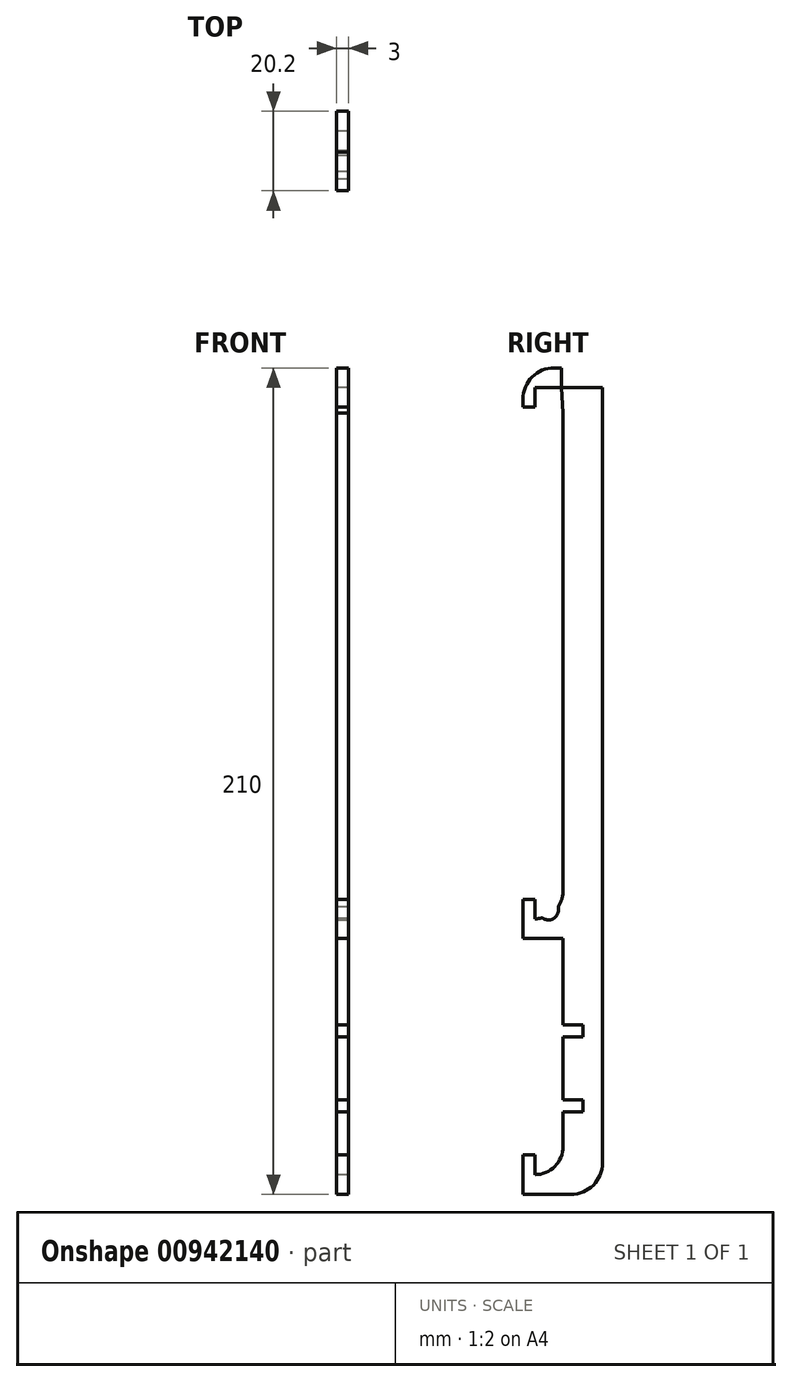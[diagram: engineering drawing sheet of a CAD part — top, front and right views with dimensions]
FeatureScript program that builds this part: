
annotation { "Feature Type Name" : "Feature", "Feature Type Description" : "" }
export const myFeature = defineFeature(function(context is Context, id is Id, definition is map)
    precondition{}
    {
        {
            var Q0;
            Q0=qCreatedBy(makeId("Right.planeOp"),FACE);
            var sketch = newSketch(context, id + "F0", { "sketchPlane" : qUnion([Q0])});
            skLineSegment(sketch, "E0.bottom", {"start": v(3, 0) * mm, "end": v(10.2, 0) * mm});
            skLineSegment(sketch, "E0.top", {"start": v(3, 100) * mm, "end": v(3, 100) * mm});
            skLineSegment(sketch, "E0.left", {"start": v(3, 0) * mm, "end": v(3, 100) * mm});
            skLineSegment(sketch, "E0.right", {"start": v(10.2, 0) * mm, "end": v(10.2, 92.8) * mm});
            skPoint(sketch, "E1.visualSharp", {"position": v(10.2, 100) * mm});
            skArc(sketch, "E1.filletArc", {"start": v(10.2, 92.8) * mm, "mid": v(8.1, 97.9) * mm, "end": v(3, 100) * mm});
            skLineSegment(sketch, "E2.bottom", {"start": v(0, 0) * mm, "end": v(20.2, 0) * mm});
            skLineSegment(sketch, "E2.top", {"start": v(0, 105) * mm, "end": v(20.2, 105) * mm});
            skLineSegment(sketch, "E2.left", {"start": v(0, 0) * mm, "end": v(0, 105) * mm});
            skLineSegment(sketch, "E2.right", {"start": v(20.2, 0) * mm, "end": v(20.2, 105) * mm});
            skLineSegment(sketch, "E3", {"start": v(0, 95) * mm, "end": v(3, 95) * mm});
            skLineSegment(sketch, "E4.bottom", {"start": v(10.2, 84) * mm, "end": v(15.2, 84) * mm});
            skLineSegment(sketch, "E4.top", {"start": v(10.2, 81) * mm, "end": v(15.2, 81) * mm});
            skLineSegment(sketch, "E4.left", {"start": v(10.2, 84) * mm, "end": v(10.2, 81) * mm});
            skLineSegment(sketch, "E4.right", {"start": v(15.2, 84) * mm, "end": v(15.2, 81) * mm});
            skLineSegment(sketch, "E5.bottom", {"start": v(10.2, 65) * mm, "end": v(15.2, 65) * mm});
            skLineSegment(sketch, "E5.top", {"start": v(10.2, 62) * mm, "end": v(15.2, 62) * mm});
            skLineSegment(sketch, "E5.left", {"start": v(10.2, 65) * mm, "end": v(10.2, 62) * mm});
            skLineSegment(sketch, "E5.right", {"start": v(15.2, 65) * mm, "end": v(15.2, 62) * mm});
            skSolve(sketch);
        }
        {
            var Q0;
            {var subQ1=sQuery(id+"F0.wireOp",EDGE,"E0.right");Q0=makeQuery(id+"F0.imprint","IMPRINT",FACE,{"disambiguationData":[TD([[makeQuery(id+"F0.imprint","IMPRINT",EDGE,{"derivedFrom":subQ1}),-1.0]])]});}
            extrude(context, id + "F1", {"entities" : qUnion([Q0]), "depth" : 3 * mm, "offsetDistance" : 25 * mm});
        }
        {
            var Q0;
            Q0=makeQuery(id+"F1.opExtrude","SWEPT_BODY",BODY,{"disambiguationData":[OSD([sQuery(id+"F0.wireOp",EDGE,"E0.left"),sQuery(id+"F0.wireOp",EDGE,"E0.right"),sQuery(id+"F0.wireOp",EDGE,"E1.filletArc"),sQuery(id+"F0.wireOp",EDGE,"E2.bottom"),sQuery(id+"F0.wireOp",EDGE,"E2.top"),sQuery(id+"F0.wireOp",EDGE,"E2.left"),sQuery(id+"F0.wireOp",EDGE,"E2.right"),sQuery(id+"F0.wireOp",EDGE,"E3")])]});
            var Q1;
            Q1=qCreatedBy(makeId("Top.planeOp"),FACE);
            mirror(context, id + "F2", {"operationType" : NewBodyOperationType.ADD, "entities" : qUnion([Q0]), "mirrorPlane" : qUnion([Q1])});
        }
        {
            var Q0;
            Q0=qCreatedBy(makeId("Right.planeOp"),FACE);
            var sketch = newSketch(context, id + "F3", { "sketchPlane" : qUnion([Q0])});
            skArc(sketch, "E6.0", {"start": v(10.2, 92.8) * mm, "mid": v(8.1, 97.9) * mm, "end": v(3, 100) * mm});
            skLineSegment(sketch, "E7.0", {"start": v(3, 0) * mm, "end": v(3, 100) * mm});
            skLineSegment(sketch, "E8.0", {"start": v(0, 95) * mm, "end": v(3, 95) * mm});
            skLineSegment(sketch, "E9.0", {"start": v(0, 0) * mm, "end": v(0, 105) * mm});
            skLineSegment(sketch, "E10.0", {"start": v(0, 105) * mm, "end": v(20.2, 105) * mm});
            skLineSegment(sketch, "E11.0", {"start": v(10.2, 0) * mm, "end": v(10.2, 92.8) * mm});
            skLineSegment(sketch, "E12.0", {"start": v(20.2, 0) * mm, "end": v(20.2, 105) * mm});
            skLineSegment(sketch, "E13.0", {"start": v(15.2, 84) * mm, "end": v(15.2, 81) * mm});
            skLineSegment(sketch, "E14", {"start": v(15.2, 84) * mm, "end": v(20.2, 84) * mm});
            skLineSegment(sketch, "E15", {"start": v(15.2, 81) * mm, "end": v(20.2, 81) * mm});
            skLineSegment(sketch, "E16", {"start": v(10.2, 32.5) * mm, "end": v(20.2, 32.5) * mm});
            skSolve(sketch);
        }
        {
            var Q0;
            {var subQ6=sQuery(id+"F3.wireOp",EDGE,"E6.0");Q0=makeQuery(id+"F3.imprint","IMPRINT",FACE,{"disambiguationData":[TD([[makeQuery(id+"F3.imprint","IMPRINT",EDGE,{"derivedFrom":subQ6}),-1.0]])]});}
            extrude(context, id + "F4", {"entities" : qUnion([Q0]), "depth" : 3 * mm, "offsetDistance" : 25 * mm});
        }
        {
            var Q0;
            Q0=makeQuery(id+"F4.opExtrude","SWEPT_BODY",BODY,{"disambiguationData":[OSD([sQuery(id+"F3.wireOp",EDGE,"E6.0"),sQuery(id+"F3.wireOp",EDGE,"E7.0"),sQuery(id+"F3.wireOp",EDGE,"E8.0"),sQuery(id+"F3.wireOp",EDGE,"E9.0"),sQuery(id+"F3.wireOp",EDGE,"E10.0"),sQuery(id+"F3.wireOp",EDGE,"E11.0"),sQuery(id+"F3.wireOp",EDGE,"E12.0"),sQuery(id+"F3.wireOp",EDGE,"E13.0"),sQuery(id+"F3.wireOp",EDGE,"E14"),sQuery(id+"F3.wireOp",EDGE,"E15"),sQuery(id+"F3.wireOp",EDGE,"E16")])]});
            var Q1;
            Q1=makeQuery(id+"F4.opExtrude","SWEPT_FACE",FACE,{"disambiguationData":[OSD([sQuery(id+"F3.wireOp",EDGE,"E16")])]});
            mirror(context, id + "F5", {"operationType" : NewBodyOperationType.ADD, "entities" : qUnion([Q0]), "mirrorPlane" : qUnion([Q1])});
        }
        {
            var Q0;
            Q0=qCreatedBy(makeId("Right.planeOp"),FACE);
            var sketch = newSketch(context, id + "F6", { "sketchPlane" : qUnion([Q0])});
            skLineSegment(sketch, "E17.0", {"start": v(0, 105) * mm, "end": v(20.2, 105) * mm});
            skCircle(sketch, "E18", {"center": v(21, 113) * mm, "radius": 2.6 * mm});
            skCircle(sketch, "E19", {"center": v(21, 113) * mm, "radius": 6.75 * mm});
            skLineSegment(sketch, "E20", {"start": v(0, 105) * mm, "end": v(16.81, 118.3) * mm});
            skLineSegment(sketch, "E21", {"start": v(20.2, 105) * mm, "end": v(24.08, 107) * mm});
            skSolve(sketch);
        }
        {
            var Q0;
            Q0=makeQuery(id+"F6.imprint","IMPRINT",FACE,{"disambiguationData":[TD([[makeQuery(id+"F6.imprint","IMPRINT",EDGE,{"derivedFrom":sQuery(id+"F6.wireOp",EDGE,"E17.0")}),1.0]])]});
            var Q1;
            Q1=makeQuery(id+"F6.imprint","IMPRINT",FACE,{"disambiguationData":[TD([[makeQuery(id+"F6.imprint","IMPRINT",EDGE,{"derivedFrom":sQuery(id+"F6.wireOp",EDGE,"E18")}),-1.0]])]});
            var Q2;
            {var subQ0=makeQuery(id+"F4.opExtrude","CAP_FACE",FACE,{"disambiguationData":[OSD([sQuery(id+"F3.wireOp",EDGE,"E6.0"),sQuery(id+"F3.wireOp",EDGE,"E7.0"),sQuery(id+"F3.wireOp",EDGE,"E8.0"),sQuery(id+"F3.wireOp",EDGE,"E9.0"),sQuery(id+"F3.wireOp",EDGE,"E10.0"),sQuery(id+"F3.wireOp",EDGE,"E11.0"),sQuery(id+"F3.wireOp",EDGE,"E12.0"),sQuery(id+"F3.wireOp",EDGE,"E13.0"),sQuery(id+"F3.wireOp",EDGE,"E14"),sQuery(id+"F3.wireOp",EDGE,"E15"),sQuery(id+"F3.wireOp",EDGE,"E16")])],"isStart":false});Q2=makeQuery(id+"F5.boolean.opBoolean","MERGE",FACE,{"derivedFrom":[subQ0,makeQuery(id+"F5.opPattern","COPY",FACE,{"derivedFrom":subQ0,"instanceName":"1"})]});}
            extrude(context, id + "F7", {"entities" : qUnion([Q0, Q1]), "operationType" : NewBodyOperationType.ADD, "endBound" : BoundingType.UP_TO_SURFACE, "depth" : 25 * mm, "endBoundEntityFace" : qUnion([Q2]), "offsetDistance" : 25 * mm});
        }
        {
            var Q0;
            {var subQ0=makeQuery(id+"F1.opExtrude","CAP_FACE",FACE,{"disambiguationData":[OSD([sQuery(id+"F0.wireOp",EDGE,"E0.left"),sQuery(id+"F0.wireOp",EDGE,"E0.right"),sQuery(id+"F0.wireOp",EDGE,"E1.filletArc"),sQuery(id+"F0.wireOp",EDGE,"E2.bottom"),sQuery(id+"F0.wireOp",EDGE,"E2.top"),sQuery(id+"F0.wireOp",EDGE,"E2.left"),sQuery(id+"F0.wireOp",EDGE,"E2.right"),sQuery(id+"F0.wireOp",EDGE,"E3"),sQuery(id+"F0.wireOp",EDGE,"E4.bottom"),sQuery(id+"F0.wireOp",EDGE,"E4.top"),sQuery(id+"F0.wireOp",EDGE,"E4.right"),sQuery(id+"F0.wireOp",EDGE,"vDQWWtUP-PzlS-vFGq-nPRO-Mq5S4r9yg4Yc.bottom"),sQuery(id+"F0.wireOp",EDGE,"vDQWWtUP-PzlS-vFGq-nPRO-Mq5S4r9yg4Yc.top"),sQuery(id+"F0.wireOp",EDGE,"vDQWWtUP-PzlS-vFGq-nPRO-Mq5S4r9yg4Yc.right")])],"isStart":false});Q0=makeQuery(id+"F2.boolean.opBoolean","MERGE",FACE,{"derivedFrom":[subQ0,makeQuery(id+"F2.opPattern","COPY",FACE,{"derivedFrom":subQ0,"instanceName":"1"})]});}
            var sketch = newSketch(context, id + "F8", { "sketchPlane" : qUnion([Q0])});
            skLineSegment(sketch, "E22", {"start": v(10.2, 92.8) * mm, "end": v(9.82, 100) * mm});
            skLineSegment(sketch, "E23", {"start": v(9.82, 105) * mm, "end": v(0, 105) * mm});
            skLineSegment(sketch, "E24", {"start": v(0, 105) * mm, "end": v(0, 92.8) * mm});
            skLineSegment(sketch, "E25", {"start": v(0, 92.8) * mm, "end": v(10.2, 92.8) * mm});
            skLineSegment(sketch, "E26", {"start": v(9.82, 100) * mm, "end": v(9.82, 105) * mm});
            skLineSegment(sketch, "E27", {"start": v(3, 100) * mm, "end": v(9.82, 100) * mm});
            skLineSegment(sketch, "E28", {"start": v(9.82, 100) * mm, "end": v(20.2, 100) * mm});
            skLineSegment(sketch, "E29", {"start": v(20.2, 100) * mm, "end": v(20.2, 105) * mm});
            skLineSegment(sketch, "E30", {"start": v(20.2, 105) * mm, "end": v(9.82, 105) * mm});
            skSolve(sketch);
        }
        {
            var Q0;
            {var subQ1=sQuery(id+"F8.wireOp",EDGE,"E23");Q0=makeQuery(id+"F8.imprint","IMPRINT",FACE,{"disambiguationData":[TD([[makeQuery(id+"F8.imprint","IMPRINT",EDGE,{"derivedFrom":subQ1}),-1.0]])]});}
            var Q1;
            {var subQ3=sQuery(id+"F8.wireOp",EDGE,"E26");Q1=makeQuery(id+"F8.imprint","IMPRINT",FACE,{"disambiguationData":[TD([[makeQuery(id+"F8.imprint","IMPRINT",EDGE,{"derivedFrom":subQ3}),-1.0]])]});}
            var Q2;
            {var subQ0=sQuery(id+"F8.wireOp",EDGE,"E27");Q2=makeQuery(id+"F8.imprint","IMPRINT",FACE,{"disambiguationData":[TD([[makeQuery(id+"F8.imprint","IMPRINT",EDGE,{"derivedFrom":subQ0}),-1.0]])]});}
            extrude(context, id + "F9", {"entities" : qUnion([Q0, Q1, Q2]), "operationType" : NewBodyOperationType.REMOVE, "endBound" : BoundingType.UP_TO_NEXT, "oppositeDirection" : true, "depth" : 25 * mm, "offsetDistance" : 25 * mm});
        }
        {
            var Q0;
            {var subQ0=makeQuery(id+"F4.opExtrude","CAP_FACE",FACE,{"disambiguationData":[OSD([sQuery(id+"F3.wireOp",EDGE,"E6.0"),sQuery(id+"F3.wireOp",EDGE,"E7.0"),sQuery(id+"F3.wireOp",EDGE,"E8.0"),sQuery(id+"F3.wireOp",EDGE,"E9.0"),sQuery(id+"F3.wireOp",EDGE,"E10.0"),sQuery(id+"F3.wireOp",EDGE,"E11.0"),sQuery(id+"F3.wireOp",EDGE,"E12.0"),sQuery(id+"F3.wireOp",EDGE,"E13.0"),sQuery(id+"F3.wireOp",EDGE,"E14"),sQuery(id+"F3.wireOp",EDGE,"E15"),sQuery(id+"F3.wireOp",EDGE,"E16")])],"isStart":false});Q0=makeQuery(id+"F7.boolean.opBoolean","MERGE",FACE,{"derivedFrom":[makeQuery(id+"F5.boolean.opBoolean","MERGE",FACE,{"derivedFrom":[subQ0,makeQuery(id+"F5.opPattern","COPY",FACE,{"derivedFrom":subQ0,"instanceName":"1"})]}),makeQuery(id+"F7.opExtrude","CAP_FACE",FACE,{"disambiguationData":[OSD([sQuery(id+"F6.wireOp",EDGE,"E17.0"),sQuery(id+"F6.wireOp",EDGE,"E18"),sQuery(id+"F6.wireOp",EDGE,"E19"),sQuery(id+"F6.wireOp",EDGE,"E20"),sQuery(id+"F6.wireOp",EDGE,"E21")])],"isStart":false})]});}
            var sketch = newSketch(context, id + "F10", { "sketchPlane" : qUnion([Q0])});
            skCircle(sketch, "E31", {"center": v(6.5, -31.78) * mm, "radius": 2.5 * mm});
            skLineSegment(sketch, "E32", {"start": v(9, -31.78) * mm, "end": v(6.5, -31.78) * mm});
            skCircle(sketch, "E33", {"center": v(6.5, -32.78) * mm, "radius": 2.5 * mm});
            skLineSegment(sketch, "E34", {"start": v(9, -31.78) * mm, "end": v(9, -32.78) * mm});
            skSolve(sketch);
        }
        {
            var Q0;
            {var subQ0=sQuery(id+"F10.wireOp",EDGE,"E33");var subQ1=sQuery(id+"F10.wireOp",EDGE,"E31");var subQ2=makeQuery(id+"F10.imprint","INTERSECT",VERTEX,{"disambiguationData":[OD(1.0)],"derivedFrom":[subQ1,subQ0]});Q0=makeQuery(id+"F10.imprint","IMPRINT",FACE,{"disambiguationData":[TD([[makeQuery(id+"F10.imprint","IMPRINT",EDGE,{"disambiguationData":[TD([[subQ2,1.0]])],"derivedFrom":subQ1}),-1.0]])]});}
            var Q1;
            {var subQ0=sQuery(id+"F10.wireOp",EDGE,"E33");var subQ1=sQuery(id+"F10.wireOp",EDGE,"E31");var subQ2=makeQuery(id+"F10.imprint","INTERSECT",VERTEX,{"disambiguationData":[OD(1.0)],"derivedFrom":[subQ1,subQ0]});Q1=makeQuery(id+"F10.imprint","IMPRINT",FACE,{"disambiguationData":[TD([[makeQuery(id+"F10.imprint","IMPRINT",EDGE,{"disambiguationData":[TD([[subQ2,1.0]])],"derivedFrom":subQ1}),1.0]])]});}
            var Q2;
            {var subQ0=sQuery(id+"F10.wireOp",EDGE,"E31");var subQ3=sQuery(id+"F10.wireOp",EDGE,"E33");var subQ4=makeQuery(id+"F10.imprint","INTERSECT",VERTEX,{"disambiguationData":[OD(1.0)],"derivedFrom":[subQ0,subQ3]});Q2=makeQuery(id+"F10.imprint","IMPRINT",FACE,{"disambiguationData":[TD([[makeQuery(id+"F10.imprint","IMPRINT",EDGE,{"disambiguationData":[TD([[subQ4,-1.0]])],"derivedFrom":subQ3}),-1.0]])]});}
            var Q3;
            {var subQ0=sQuery(id+"F10.wireOp",EDGE,"E34");Q3=makeQuery(id+"F10.imprint","IMPRINT",FACE,{"disambiguationData":[TD([[makeQuery(id+"F10.imprint","IMPRINT",EDGE,{"derivedFrom":subQ0}),-1.0]])]});}
            extrude(context, id + "F11", {"entities" : qUnion([Q0, Q1, Q2, Q3]), "operationType" : NewBodyOperationType.REMOVE, "endBound" : BoundingType.THROUGH_ALL, "oppositeDirection" : true, "depth" : 25 * mm, "offsetDistance" : 25 * mm});
        }
        {
            var Q0;
            Q0=makeQuery(id+"F7.boolean.opBoolean","MERGE",EDGE,{"derivedFrom":[makeQuery(id+"F4.opExtrude","SWEPT_EDGE",EDGE,{"disambiguationData":[OSD([sQuery(id+"F3.wireOp",EDGE,"E9.0"),sQuery(id+"F3.wireOp",EDGE,"E10.0")])]}),makeQuery(id+"F7.opExtrude","SWEPT_EDGE",EDGE,{"disambiguationData":[OSD([sQuery(id+"F6.wireOp",EDGE,"E17.0"),sQuery(id+"F6.wireOp",EDGE,"E20")])]})]});
            var Q1;
            Q1=makeQuery(id+"F7.boolean.opBoolean","MERGE",EDGE,{"derivedFrom":[makeQuery(id+"F4.opExtrude","SWEPT_EDGE",EDGE,{"disambiguationData":[OSD([sQuery(id+"F3.wireOp",EDGE,"E10.0"),sQuery(id+"F3.wireOp",EDGE,"E12.0")])]}),makeQuery(id+"F7.opExtrude","SWEPT_EDGE",EDGE,{"disambiguationData":[OSD([sQuery(id+"F6.wireOp",EDGE,"E17.0"),sQuery(id+"F6.wireOp",EDGE,"E21")])]})]});
            var Q2;
            Q2=makeQuery(id+"F9.boolean.opBoolean","COPY",EDGE,{"derivedFrom":makeQuery(id+"F9.opExtrude","SWEPT_EDGE",EDGE,{"disambiguationData":[OSD([sQuery(id+"F0.wireOp",EDGE,"E2.right"),sQuery(id+"F8.wireOp",EDGE,"E28"),sQuery(id+"F8.wireOp",EDGE,"E29")])]})});
            var Q3;
            Q3=makeQuery(id+"F5.opPattern","COPY",EDGE,{"derivedFrom":makeQuery(id+"F4.opExtrude","SWEPT_EDGE",EDGE,{"disambiguationData":[OSD([sQuery(id+"F3.wireOp",EDGE,"E10.0"),sQuery(id+"F3.wireOp",EDGE,"E12.0")])]}),"instanceName":"1"});
            var Q4;
            Q4=makeQuery(id+"F2.opPattern","COPY",EDGE,{"derivedFrom":makeQuery(id+"F1.opExtrude","SWEPT_EDGE",EDGE,{"disambiguationData":[OSD([sQuery(id+"F0.wireOp",EDGE,"E2.top"),sQuery(id+"F0.wireOp",EDGE,"E2.right")])]}),"instanceName":"1"});
            fillet(context, id + "F12", {"entities" : qUnion([Q0, Q1, Q2, Q3, Q4]), "radius" : 8 * mm, "tangentPropagation" : true, "allowEdgeOverflow" : false});
        }
    });
